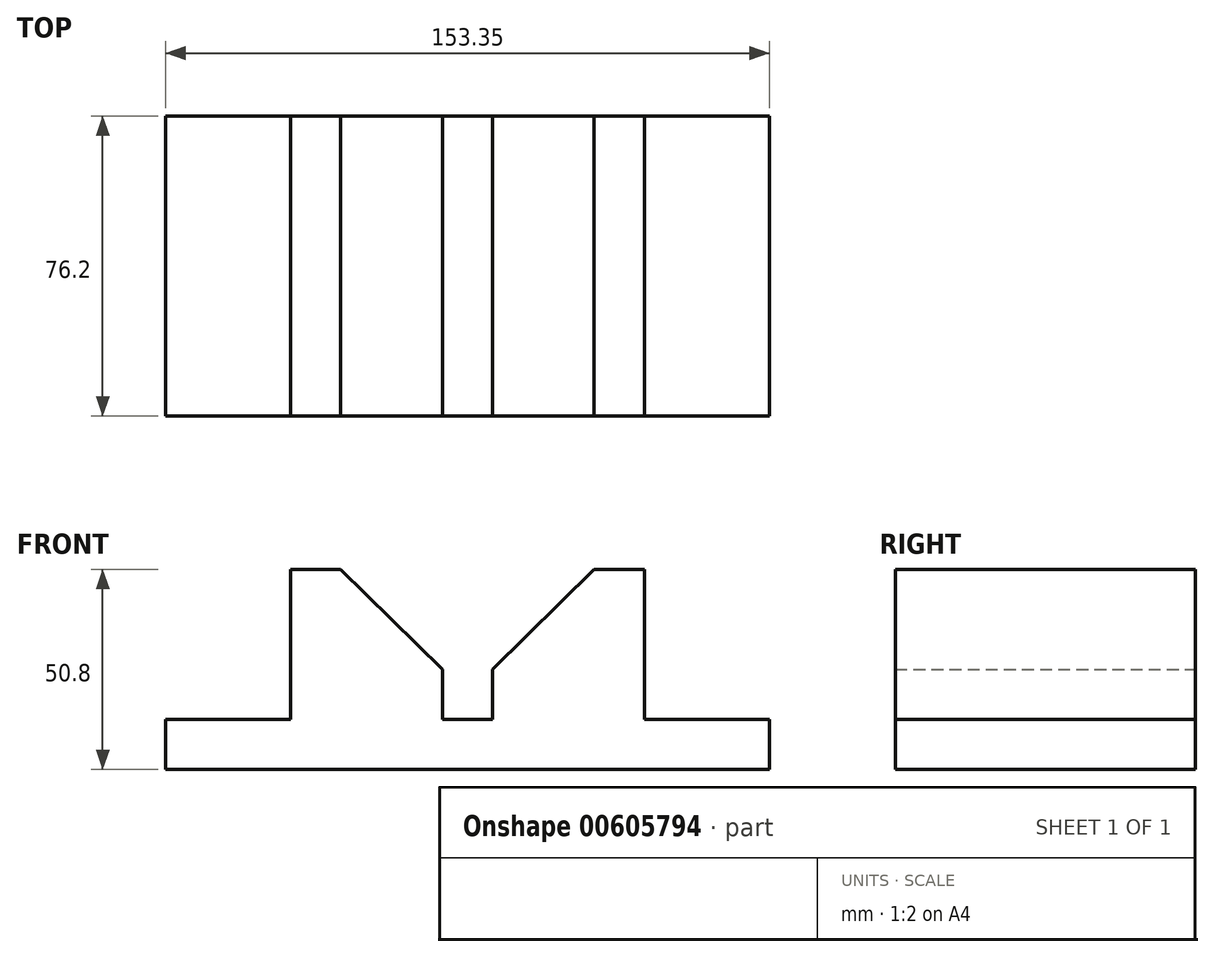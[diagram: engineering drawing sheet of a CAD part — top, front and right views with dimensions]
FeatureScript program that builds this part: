
annotation { "Feature Type Name" : "Feature", "Feature Type Description" : "" }
export const myFeature = defineFeature(function(context is Context, id is Id, definition is map)
    precondition{}
    {
        {
            var Q0;
            Q0=qCreatedBy(makeId("Front.planeOp"),FACE);
            var sketch = newSketch(context, id + "F0", { "sketchPlane" : qUnion([Q0])});
            skLineSegment(sketch, "E0", {"start": v(0, 0) * mm, "end": v(153.35, 0) * mm});
            skLineSegment(sketch, "E1", {"start": v(153.35, 0) * mm, "end": v(153.35, 12.7) * mm});
            skLineSegment(sketch, "E2", {"start": v(153.35, 12.7) * mm, "end": v(121.6, 12.7) * mm});
            skLineSegment(sketch, "E3", {"start": v(121.6, 12.7) * mm, "end": v(121.6, 50.8) * mm});
            skLineSegment(sketch, "E4", {"start": v(121.6, 50.8) * mm, "end": v(108.8, 50.8) * mm});
            skLineSegment(sketch, "E5", {"start": v(0, 0) * mm, "end": v(0, 12.7) * mm});
            skLineSegment(sketch, "E6", {"start": v(0, 12.7) * mm, "end": v(31.75, 12.7) * mm});
            skLineSegment(sketch, "E7", {"start": v(31.75, 12.7) * mm, "end": v(31.75, 50.8) * mm});
            skLineSegment(sketch, "E8", {"start": v(31.75, 50.8) * mm, "end": v(44.45, 50.8) * mm});
            skLineSegment(sketch, "E9", {"start": v(76.68, 12.7) * mm, "end": v(70.33, 12.7) * mm});
            skLineSegment(sketch, "E10", {"start": v(76.68, 12.7) * mm, "end": v(83.03, 12.7) * mm});
            skLineSegment(sketch, "E11", {"start": v(70.33, 12.7) * mm, "end": v(70.33, 25.4) * mm});
            skLineSegment(sketch, "E12", {"start": v(83.03, 12.7) * mm, "end": v(83.03, 25.4) * mm});
            skLineSegment(sketch, "E13", {"start": v(44.45, 50.8) * mm, "end": v(70.33, 25.4) * mm});
            skLineSegment(sketch, "E14", {"start": v(108.8, 50.8) * mm, "end": v(83.03, 25.4) * mm});
            skSolve(sketch);
        }
        {
            var Q0;
            Q0=makeQuery(id+"F0.imprint","IMPRINT",FACE,{"disambiguationData":[TD([[makeQuery(id+"F0.imprint","IMPRINT",EDGE,{"derivedFrom":sQuery(id+"F0.wireOp",EDGE,"E0")}),1.0]])]});
            extrude(context, id + "F1", {"entities" : qUnion([Q0]), "depth" : 76.2 * mm, "offsetDistance" : 25.4 * mm});
        }
    });
